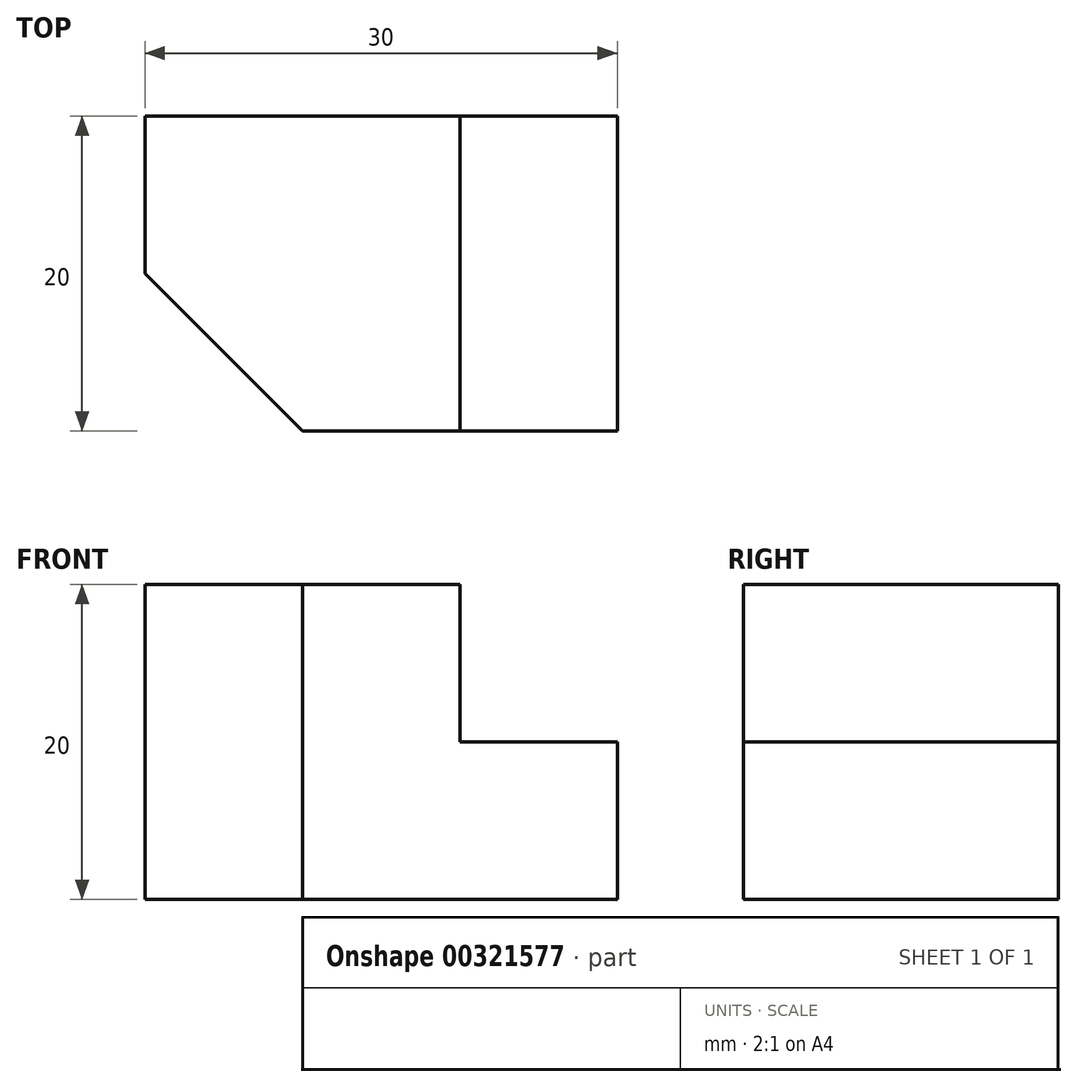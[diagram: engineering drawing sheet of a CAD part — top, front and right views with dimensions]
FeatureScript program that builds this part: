
annotation { "Feature Type Name" : "Feature", "Feature Type Description" : "" }
export const myFeature = defineFeature(function(context is Context, id is Id, definition is map)
    precondition{}
    {
        {
            var Q0;
            Q0=qCreatedBy(makeId("Top.planeOp"),FACE);
            var sketch = newSketch(context, id + "F0", { "sketchPlane" : qUnion([Q0])});
            skLineSegment(sketch, "E0.bottom", {"start": v(0, 0) * mm, "end": v(10, 0) * mm});
            skLineSegment(sketch, "E0.top", {"start": v(0, 20) * mm, "end": v(10, 20) * mm});
            skLineSegment(sketch, "E0.left", {"start": v(0, 0) * mm, "end": v(0, 20) * mm});
            skLineSegment(sketch, "E0.right", {"start": v(10, 0) * mm, "end": v(10, 20) * mm});
            skLineSegment(sketch, "E1", {"start": v(0, 0) * mm, "end": v(-10, 0) * mm});
            skLineSegment(sketch, "E2", {"start": v(-10, 0) * mm, "end": v(-20, 10) * mm});
            skLineSegment(sketch, "E3", {"start": v(-20, 10) * mm, "end": v(-20, 20) * mm});
            skLineSegment(sketch, "E4", {"start": v(-20, 20) * mm, "end": v(0, 20) * mm});
            skSolve(sketch);
        }
        {
            var Q0;
            Q0 = qSketchRegion(id + "F0", true);
            extrude(context, id + "F1", {"entities" : qUnion([Q0]), "depth" : 20 * mm});
        }
        {
            var Q0;
            Q0=makeQuery(id+"F1.opExtrude","SWEPT_FACE",FACE,{"disambiguationData":[OSD([sQuery(id+"F0.wireOp",EDGE,"E0.bottom"),sQuery(id+"F0.wireOp",EDGE,"E1")])]});
            var sketch = newSketch(context, id + "F2", { "sketchPlane" : qUnion([Q0])});
            skLineSegment(sketch, "E5.bottom", {"start": v(10, 20) * mm, "end": v(0, 20) * mm});
            skLineSegment(sketch, "E5.top", {"start": v(10, 10) * mm, "end": v(0, 10) * mm});
            skLineSegment(sketch, "E5.left", {"start": v(10, 20) * mm, "end": v(10, 10) * mm});
            skLineSegment(sketch, "E5.right", {"start": v(0, 20) * mm, "end": v(0, 10) * mm});
            skSolve(sketch);
        }
        {
            var Q0;
            Q0 = qSketchRegion(id + "F2", true);
            extrude(context, id + "F3", {"entities" : qUnion([Q0]), "operationType" : NewBodyOperationType.REMOVE, "endBound" : BoundingType.THROUGH_ALL, "oppositeDirection" : true, "depth" : 25 * mm});
        }
    });
